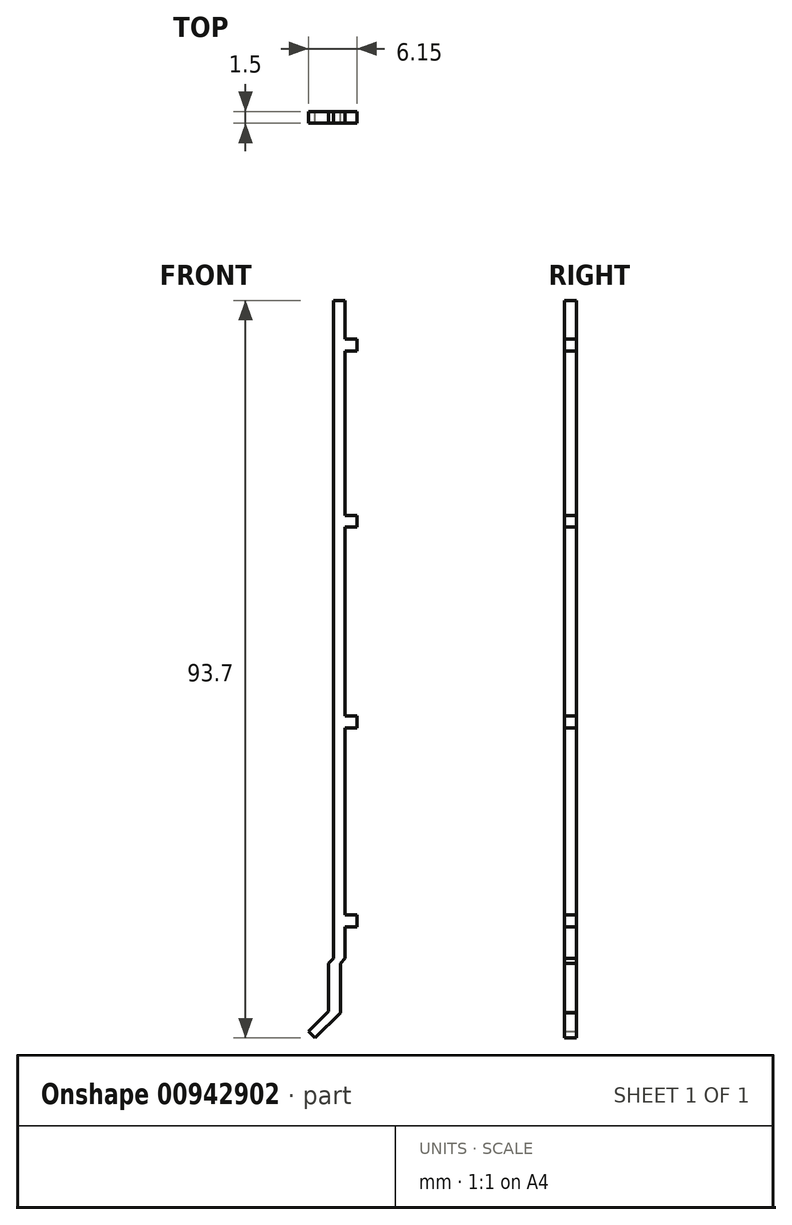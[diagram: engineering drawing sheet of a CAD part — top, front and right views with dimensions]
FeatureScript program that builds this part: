
annotation { "Feature Type Name" : "Feature", "Feature Type Description" : "" }
export const myFeature = defineFeature(function(context is Context, id is Id, definition is map)
    precondition{}
    {
        {
            var Q0;
            Q0=qCreatedBy(makeId("Front.planeOp"),FACE);
            var sketch = newSketch(context, id + "F0", { "sketchPlane" : qUnion([Q0])});
            skLineSegment(sketch, "E0", {"start": v(-53.58, -58.1) * mm, "end": v(-50.38, -54.9) * mm});
            skLineSegment(sketch, "E1", {"start": v(-50.38, -54.9) * mm, "end": v(-50.38, -48.6) * mm});
            skLineSegment(sketch, "E2", {"start": v(-49.78, -48) * mm, "end": v(-50.38, -48.6) * mm});
            skLineSegment(sketch, "E3", {"start": v(-53.58, -58.1) * mm, "end": v(-54.43, -57.24) * mm});
            skLineSegment(sketch, "E4", {"start": v(-51.88, -48.6) * mm, "end": v(-51.88, -54.7) * mm});
            skLineSegment(sketch, "E5", {"start": v(-51.28, -48) * mm, "end": v(-51.28, 35.6) * mm});
            skLineSegment(sketch, "E6", {"start": v(-51.28, 35.6) * mm, "end": v(-49.78, 35.6) * mm});
            skLineSegment(sketch, "E7", {"start": v(-51.28, -48) * mm, "end": v(-51.88, -48.6) * mm});
            skLineSegment(sketch, "E8", {"start": v(-49.78, -48) * mm, "end": v(-49.78, 35.6) * mm});
            skLineSegment(sketch, "E9", {"start": v(-51.88, -54.7) * mm, "end": v(-54.43, -57.24) * mm});
            skLineSegment(sketch, "E10.bottom", {"start": v(-49.78, -42.47) * mm, "end": v(-48.28, -42.47) * mm});
            skLineSegment(sketch, "E10.top", {"start": v(-49.78, -43.97) * mm, "end": v(-48.28, -43.97) * mm});
            skLineSegment(sketch, "E10.left", {"start": v(-49.78, -42.47) * mm, "end": v(-49.78, -43.97) * mm});
            skLineSegment(sketch, "E10.right", {"start": v(-48.28, -42.47) * mm, "end": v(-48.28, -43.97) * mm});
            skLineSegment(sketch, "E11.bottom", {"start": v(-49.78, 30.7) * mm, "end": v(-48.28, 30.7) * mm});
            skLineSegment(sketch, "E11.top", {"start": v(-49.78, 29.2) * mm, "end": v(-48.28, 29.2) * mm});
            skLineSegment(sketch, "E11.left", {"start": v(-49.78, 30.7) * mm, "end": v(-49.78, 29.2) * mm});
            skLineSegment(sketch, "E11.right", {"start": v(-48.28, 30.7) * mm, "end": v(-48.28, 29.2) * mm});
            skLineSegment(sketch, "E12.bottom", {"start": v(-49.78, 8.32) * mm, "end": v(-48.28, 8.32) * mm});
            skLineSegment(sketch, "E12.top", {"start": v(-49.78, 6.82) * mm, "end": v(-48.28, 6.82) * mm});
            skLineSegment(sketch, "E12.left", {"start": v(-49.78, 8.32) * mm, "end": v(-49.78, 6.82) * mm});
            skLineSegment(sketch, "E12.right", {"start": v(-48.28, 8.32) * mm, "end": v(-48.28, 6.82) * mm});
            skLineSegment(sketch, "E13.left", {"start": v(-49.78, -12.3) * mm, "end": v(-49.78, -13.8) * mm});
            skLineSegment(sketch, "E14.bottom", {"start": v(-49.78, -17.19) * mm, "end": v(-48.28, -17.19) * mm});
            skLineSegment(sketch, "E14.top", {"start": v(-49.78, -18.69) * mm, "end": v(-48.28, -18.69) * mm});
            skLineSegment(sketch, "E14.left", {"start": v(-49.78, -17.19) * mm, "end": v(-49.78, -18.69) * mm});
            skLineSegment(sketch, "E14.right", {"start": v(-48.28, -17.19) * mm, "end": v(-48.28, -18.69) * mm});
            skLineSegment(sketch, "E15", {"start": v(-53.58, -58.1) * mm, "end": v(-32.32, -58.1) * mm, "construction": true});
            skLineSegment(sketch, "E16", {"start": v(-50.38, -54.9) * mm, "end": v(-32.32, -54.9) * mm, "construction": true});
            skLineSegment(sketch, "E17", {"start": v(-50.38, -48.6) * mm, "end": v(-32.32, -48.6) * mm, "construction": true});
            skLineSegment(sketch, "E18", {"start": v(-49.78, 35.6) * mm, "end": v(-32.32, 35.6) * mm, "construction": true});
            skSolve(sketch);
        }
        {
            var Q0;
            Q0=makeQuery(id+"F0.imprint","IMPRINT",FACE,{"disambiguationData":[TD([[makeQuery(id+"F0.imprint","IMPRINT",EDGE,{"derivedFrom":sQuery(id+"F0.wireOp",EDGE,"E0")}),1.0]])]});
            var Q1;
            Q1=makeQuery(id+"F0.imprint","IMPRINT",FACE,{"disambiguationData":[TD([[makeQuery(id+"F0.imprint","IMPRINT",EDGE,{"derivedFrom":sQuery(id+"F0.wireOp",EDGE,"E10.bottom")}),-1.0]])]});
            var Q2;
            Q2=makeQuery(id+"F0.imprint","IMPRINT",FACE,{"disambiguationData":[TD([[makeQuery(id+"F0.imprint","IMPRINT",EDGE,{"derivedFrom":sQuery(id+"F0.wireOp",EDGE,"E14.bottom")}),-1.0]])]});
            var Q3;
            Q3=makeQuery(id+"F0.imprint","IMPRINT",FACE,{"disambiguationData":[TD([[makeQuery(id+"F0.imprint","IMPRINT",EDGE,{"derivedFrom":sQuery(id+"F0.wireOp",EDGE,"E11.bottom")}),-1.0]])]});
            var Q4;
            Q4=makeQuery(id+"F0.imprint","IMPRINT",FACE,{"disambiguationData":[TD([[makeQuery(id+"F0.imprint","IMPRINT",EDGE,{"derivedFrom":sQuery(id+"F0.wireOp",EDGE,"E12.bottom")}),-1.0]])]});
            extrude(context, id + "F1", {"entities" : qUnion([Q0, Q1, Q2, Q3, Q4]), "endBound" : BoundingType.SYMMETRIC, "depth" : 1.5 * mm, "offsetDistance" : 25 * mm});
        }
    });
